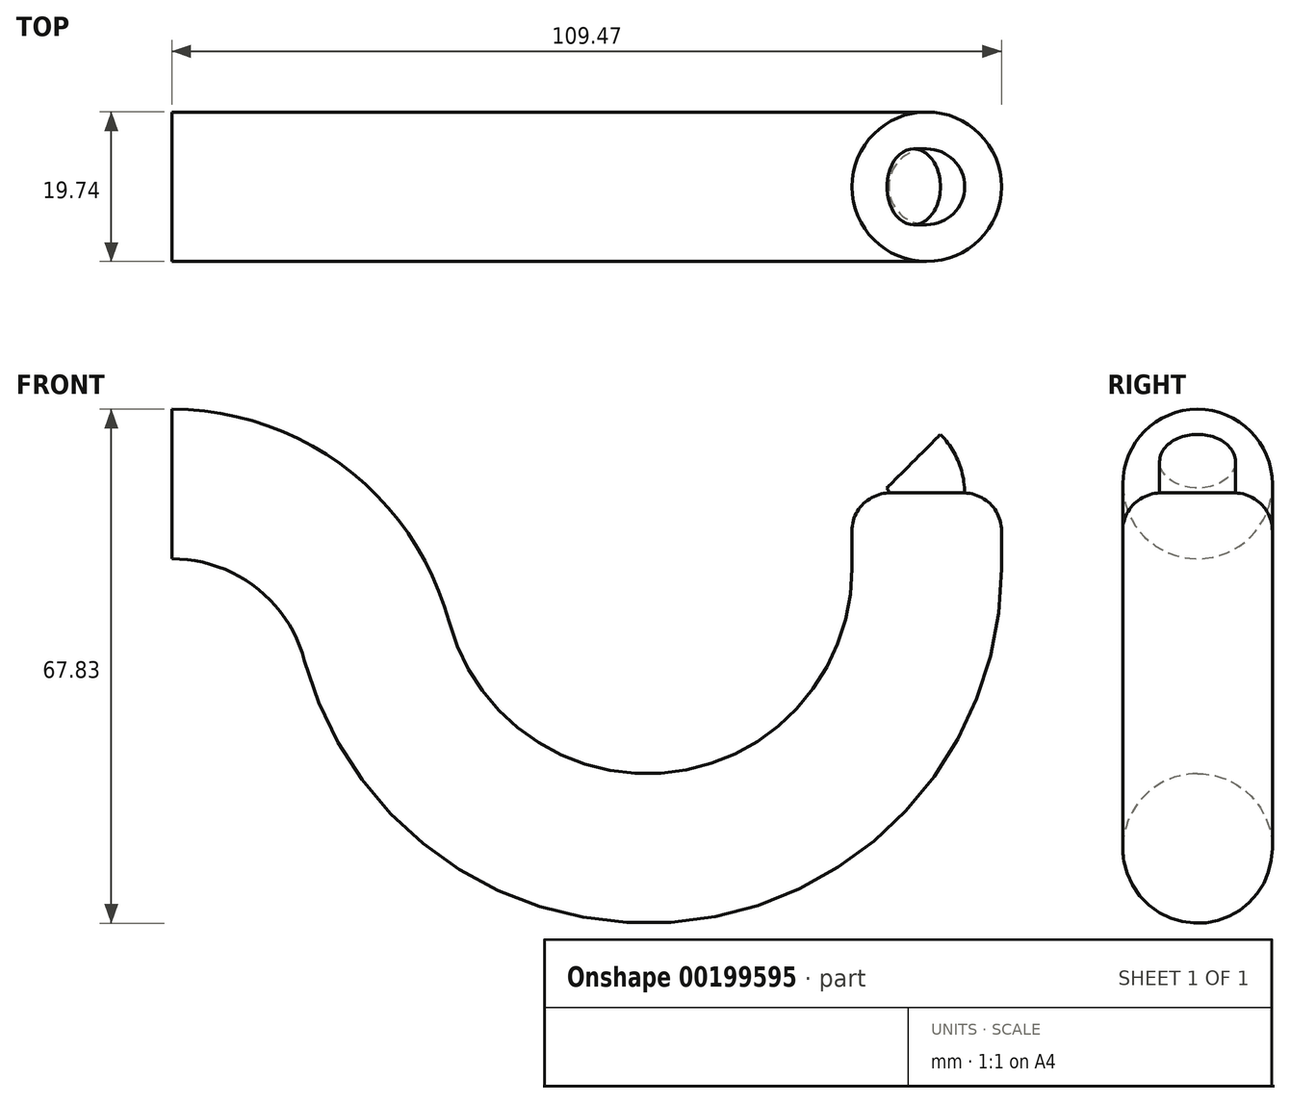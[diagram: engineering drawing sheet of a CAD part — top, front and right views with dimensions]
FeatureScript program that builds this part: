
annotation { "Feature Type Name" : "Feature", "Feature Type Description" : "" }
export const myFeature = defineFeature(function(context is Context, id is Id, definition is map)
    precondition{}
    {
        {
            var Q0;
            Q0=qCreatedBy(makeId("Top.planeOp"),FACE);
            var sketch = newSketch(context, id + "F0", { "sketchPlane" : qUnion([Q0])});
            skCircle(sketch, "E0", {"center": v(17.26, 39.95) * mm, "radius": 5 * mm});
            skLineSegment(sketch, "E1", {"start": v(11.34, 46.2) * mm, "end": v(11.34, 31.4) * mm});
            skSolve(sketch);
        }
        {
            var Q0;
            Q0=makeQuery(id+"F0.imprint","IMPRINT",FACE,{"disambiguationData":[TD([[makeQuery(id+"F0.imprint","IMPRINT",EDGE,{"derivedFrom":sQuery(id+"F0.wireOp",EDGE,"E0")}),1.0]])]});
            var Q1;
            Q1=sQuery(id+"F0.wireOp",EDGE,"E1");
            revolve(context, id + "F1", {"entities" : qUnion([Q0]), "axis" : qUnion([Q1]), "revolveType" : RevolveType.TWO_DIRECTIONS, "angle" : 45 * degree, "angleBack" : 360 * degree});
        }
        {
            var Q0;
            Q0=makeQuery(id+"F1.opRevolve","CAP_FACE",FACE,{"disambiguationData":[OSD([sQuery(id+"F0.wireOp",EDGE,"E0")])],"isStart":true});
            var sketch = newSketch(context, id + "F2", { "sketchPlane" : qUnion([Q0])});
            skSolve(sketch);
        }
        {
            var Q0;
            Q0=makeQuery(id+"F2.imprint","IMPRINT",FACE,{"disambiguationData":[TD([[makeQuery(id+"F2.imprint","IMPRINT",EDGE,{"derivedFrom":makeQuery(id+"F1.opRevolve","CAP_EDGE",EDGE,{"disambiguationData":[OSD([sQuery(id+"F0.wireOp",EDGE,"E0")])],"isStart":true})}),-1.0]])]});
            var sketch = newSketch(context, id + "F3", { "sketchPlane" : qUnion([Q0])});
            skCircle(sketch, "E2", {"center": v(17.26, -39.95) * mm, "radius": 9.87 * mm});
            skSolve(sketch);
        }
        {
            var Q0;
            Q0=makeQuery(id+"F3.imprint","IMPRINT",FACE,{"disambiguationData":[TD([[makeQuery(id+"F3.imprint","IMPRINT",EDGE,{"derivedFrom":sQuery(id+"F3.wireOp",EDGE,"E2")}),1.0]])]});
            var Q1;
            Q1=makeQuery(id+"F2.imprint","IMPRINT",FACE,{"disambiguationData":[TD([[makeQuery(id+"F2.imprint","IMPRINT",EDGE,{"derivedFrom":makeQuery(id+"F1.opRevolve","CAP_EDGE",EDGE,{"disambiguationData":[OSD([sQuery(id+"F0.wireOp",EDGE,"E0")])],"isStart":true})}),-1.0]])]});
            extrude(context, id + "F4", {"entities" : qUnion([Q0, Q1]), "operationType" : NewBodyOperationType.ADD, "depth" : 10 * mm});
        }
        {
            var Q0;
            Q0=makeQuery(id+"F4.opExtrude","CAP_EDGE",EDGE,{"disambiguationData":[OSD([sQuery(id+"F3.wireOp",EDGE,"E2")])],"isStart":true});
            fillet(context, id + "F5", {"entities" : qUnion([Q0]), "radius" : 5 * mm, "tangentPropagation" : true, "allowEdgeOverflow" : false});
        }
        {
            var Q0;
            {var subQ0=sQuery(id+"F0.wireOp",EDGE,"E0");Q0=makeQuery(id+"F4.boolean.opBoolean","MERGE",FACE,{"derivedFrom":[makeQuery(id+"F4.opExtrude","CAP_FACE",FACE,{"disambiguationData":[OSD([subQ0])],"isStart":false}),makeQuery(id+"F4.opExtrude","CAP_FACE",FACE,{"disambiguationData":[OSD([subQ0,sQuery(id+"F3.wireOp",EDGE,"E2")])],"isStart":false})]});}
            var sketch = newSketch(context, id + "F6", { "sketchPlane" : qUnion([Q0])});
            skLineSegment(sketch, "E3", {"start": v(-19.65, -29.46) * mm, "end": v(-19.65, -52.9) * mm});
            skSolve(sketch);
        }
        {
            var Q0;
            Q0=makeQuery(id+"F6.imprint","IMPRINT",FACE,{"disambiguationData":[TD([[makeQuery(id+"F6.imprint","IMPRINT",EDGE,{"derivedFrom":makeQuery(id+"F4.opExtrude","CAP_EDGE",EDGE,{"disambiguationData":[OSD([sQuery(id+"F3.wireOp",EDGE,"E2")])],"isStart":false})}),1.0]])]});
            var Q1;
            Q1=sQuery(id+"F6.wireOp",EDGE,"E3");
            revolve(context, id + "F7", {"operationType" : NewBodyOperationType.ADD, "entities" : qUnion([Q0]), "axis" : qUnion([Q1]), "revolveType" : RevolveType.TWO_DIRECTIONS, "angle" : 165 * degree, "angleBack" : 360 * degree});
        }
        {
            var Q0;
            Q0=makeQuery(id+"F7.opRevolve","CAP_FACE",FACE,{"disambiguationData":[OSD([sQuery(id+"F3.wireOp",EDGE,"E2")])],"isStart":false});
            var sketch = newSketch(context, id + "F8", { "sketchPlane" : qUnion([Q0])});
            skLineSegment(sketch, "E4", {"start": v(-86.47, 49.92) * mm, "end": v(-86.47, 30.7) * mm});
            skSolve(sketch);
        }
        {
            var Q0;
            Q0=makeQuery(id+"F8.imprint","IMPRINT",FACE,{"disambiguationData":[TD([[makeQuery(id+"F8.imprint","IMPRINT",EDGE,{"derivedFrom":makeQuery(id+"F7.opRevolve","CAP_EDGE",EDGE,{"disambiguationData":[OSD([sQuery(id+"F3.wireOp",EDGE,"E2")])],"isStart":false})}),1.0]])]});
            var Q1;
            Q1=sQuery(id+"F8.wireOp",EDGE,"E4");
            revolve(context, id + "F9", {"operationType" : NewBodyOperationType.ADD, "entities" : qUnion([Q0]), "axis" : qUnion([Q1]), "revolveType" : RevolveType.ONE_DIRECTION, "angle" : 75 * degree});
        }
    });
